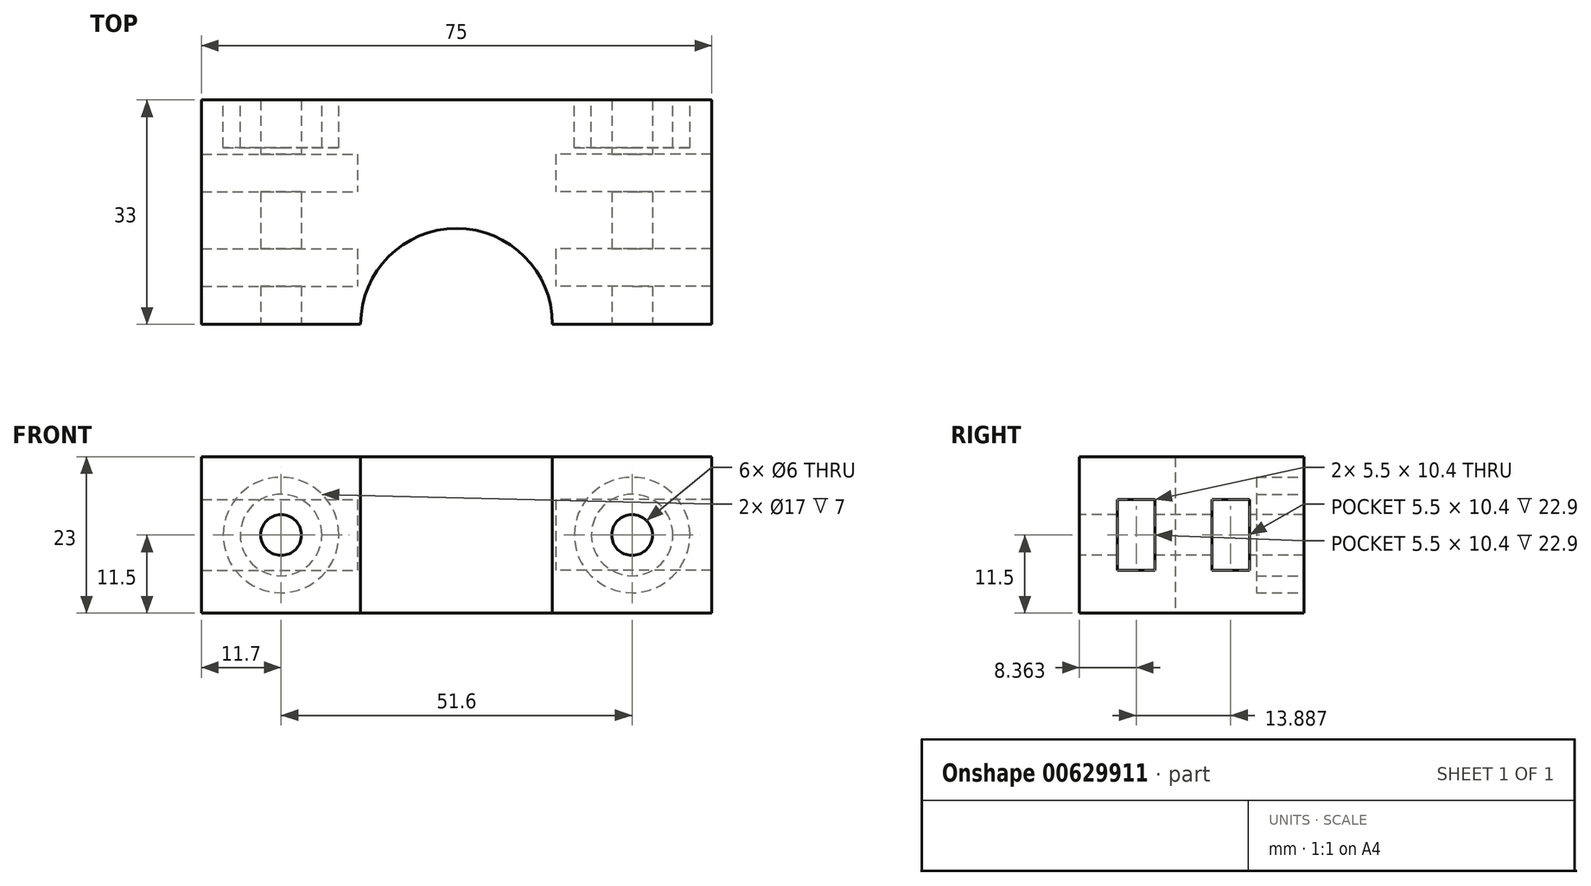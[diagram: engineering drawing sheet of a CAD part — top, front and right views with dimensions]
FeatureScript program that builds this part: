
annotation { "Feature Type Name" : "Feature", "Feature Type Description" : "" }
export const myFeature = defineFeature(function(context is Context, id is Id, definition is map)
    precondition{}
    {
        {
            var Q0;
            Q0=qCreatedBy(makeId("Top.planeOp"),FACE);
            var sketch = newSketch(context, id + "F0", { "sketchPlane" : qUnion([Q0])});
            skLineSegment(sketch, "E0.bottom", {"start": v(-37.5, 33) * mm, "end": v(37.5, 33) * mm});
            skLineSegment(sketch, "E0.top", {"start": v(-37.5, 0) * mm, "end": v(-14.1, 0) * mm});
            skLineSegment(sketch, "E0.left", {"start": v(-37.5, 33) * mm, "end": v(-37.5, 0) * mm});
            skLineSegment(sketch, "E0.right", {"start": v(37.5, 33) * mm, "end": v(37.5, 0) * mm});
            skLineSegment(sketch, "E1", {"start": v(14.1, 0) * mm, "end": v(37.5, 0) * mm});
            skArc(sketch, "E2", {"start": v(14.1, 0) * mm, "mid": v(0, 14.1) * mm, "end": v(-14.1, 0) * mm});
            skSolve(sketch);
        }
        {
            var Q0;
            Q0=makeQuery(id+"F0.imprint","IMPRINT",FACE,{"disambiguationData":[TD([[makeQuery(id+"F0.imprint","IMPRINT",EDGE,{"derivedFrom":sQuery(id+"F0.wireOp",EDGE,"E0.bottom")}),-1.0]])]});
            extrude(context, id + "F1", {"entities" : qUnion([Q0]), "depth" : 23 * mm, "offsetDistance" : 25 * mm});
        }
        {
            var Q0;
            Q0=qCreatedBy(makeId("Right.planeOp"),FACE);
            var sketch = newSketch(context, id + "F2", { "sketchPlane" : qUnion([Q0])});
            skLineSegment(sketch, "E3.bottom", {"start": v(11.11, 16.7) * mm, "end": v(5.61, 16.7) * mm});
            skLineSegment(sketch, "E3.top", {"start": v(11.11, 6.3) * mm, "end": v(5.61, 6.3) * mm});
            skLineSegment(sketch, "E3.left", {"start": v(11.11, 16.7) * mm, "end": v(11.11, 6.3) * mm});
            skLineSegment(sketch, "E3.right", {"start": v(5.61, 16.7) * mm, "end": v(5.61, 6.3) * mm});
            skLineSegment(sketch, "E4.bottom", {"start": v(25, 16.7) * mm, "end": v(19.5, 16.7) * mm});
            skLineSegment(sketch, "E4.top", {"start": v(25, 6.3) * mm, "end": v(19.5, 6.3) * mm});
            skLineSegment(sketch, "E4.left", {"start": v(25, 16.7) * mm, "end": v(25, 6.3) * mm});
            skLineSegment(sketch, "E4.right", {"start": v(19.5, 16.7) * mm, "end": v(19.5, 6.3) * mm});
            skSolve(sketch);
        }
        {
            var Q0;
            Q0=makeQuery(id+"F1.opExtrude","SWEPT_FACE",FACE,{"disambiguationData":[OSD([sQuery(id+"F0.wireOp",EDGE,"E0.top")])]});
            var sketch = newSketch(context, id + "F3", { "sketchPlane" : qUnion([Q0])});
            skLineSegment(sketch, "E5", {"start": v(-14.1, 23) * mm, "end": v(-25.8, 11.5) * mm});
            skLineSegment(sketch, "E6", {"start": v(-37.5, 0) * mm, "end": v(-37.5, 23) * mm});
            skLineSegment(sketch, "E7", {"start": v(-37.5, 23) * mm, "end": v(-14.1, 0) * mm});
            skLineSegment(sketch, "E8", {"start": v(-25.8, 11.5) * mm, "end": v(-37.5, 0) * mm});
            skCircle(sketch, "E9", {"center": v(-25.8, 11.5) * mm, "radius": 3.02 * mm});
            skSolve(sketch);
        }
        {
            var Q0;
            Q0=makeQuery(id+"F1.opExtrude","SWEPT_FACE",FACE,{"disambiguationData":[OSD([sQuery(id+"F0.wireOp",EDGE,"E1")])]});
            var sketch = newSketch(context, id + "F4", { "sketchPlane" : qUnion([Q0])});
            skLineSegment(sketch, "E10", {"start": v(14.1, 23) * mm, "end": v(37.5, 0) * mm});
            skLineSegment(sketch, "E11", {"start": v(37.5, 0) * mm, "end": v(37.5, 23) * mm});
            skLineSegment(sketch, "E12", {"start": v(37.5, 23) * mm, "end": v(14.1, 0) * mm});
            skCircle(sketch, "E13", {"center": v(25.8, 11.5) * mm, "radius": 3 * mm});
            skSolve(sketch);
        }
        {
            var Q0;
            Q0=sQuery(id+"F3.wireOp",VERTEX,"E9.center");
            var Q1;
            Q1=makeQuery(id+"F1.opExtrude","SWEPT_BODY",BODY,{"disambiguationData":[OSD([sQuery(id+"F0.wireOp",EDGE,"E0.bottom"),sQuery(id+"F0.wireOp",EDGE,"E0.top"),sQuery(id+"F0.wireOp",EDGE,"E0.left"),sQuery(id+"F0.wireOp",EDGE,"E0.right"),sQuery(id+"F0.wireOp",EDGE,"E1"),sQuery(id+"F0.wireOp",EDGE,"E2")])]});
            hole(context, id + "F5", {"style" : HoleStyle.SIMPLE, "endStyle" : HoleEndStyle.THROUGH, "holeDiameter" : 6 * mm, "majorDiameter" : 5 * mm, "isTappedThrough" : true, "tappedDepth" : 12 * mm, "tapClearance" : 3, "locations" : qUnion([Q0]), "scope" : qUnion([Q1])});
        }
        {
            var Q0;
            Q0=sQuery(id+"F4.wireOp",VERTEX,"E13.center");
            var Q1;
            Q1=makeQuery(id+"F1.opExtrude","SWEPT_BODY",BODY,{"disambiguationData":[OSD([sQuery(id+"F0.wireOp",EDGE,"E0.bottom"),sQuery(id+"F0.wireOp",EDGE,"E0.top"),sQuery(id+"F0.wireOp",EDGE,"E0.left"),sQuery(id+"F0.wireOp",EDGE,"E0.right"),sQuery(id+"F0.wireOp",EDGE,"E1"),sQuery(id+"F0.wireOp",EDGE,"E2")])]});
            hole(context, id + "F6", {"style" : HoleStyle.SIMPLE, "endStyle" : HoleEndStyle.THROUGH, "holeDiameter" : 6 * mm, "majorDiameter" : 5 * mm, "isTappedThrough" : true, "tappedDepth" : 12 * mm, "tapClearance" : 3, "locations" : qUnion([Q0]), "scope" : qUnion([Q1])});
        }
        {
            var Q0;
            Q0 = qSketchRegion(id + "F2", true);
            extrude(context, id + "F7", {"entities" : qUnion([Q0]), "operationType" : NewBodyOperationType.REMOVE, "depth" : 44.2 * mm, "offsetDistance" : 25 * mm, "hasSecondDirection" : true, "secondDirectionOppositeDirection" : false, "secondDirectionDepth" : 14.6 * mm});
        }
        {
            var Q0;
            Q0=makeQuery(id+"F1.opExtrude","SWEPT_FACE",FACE,{"disambiguationData":[OSD([sQuery(id+"F0.wireOp",EDGE,"E0.bottom")])]});
            var sketch = newSketch(context, id + "F8", { "sketchPlane" : qUnion([Q0])});
            skCircle(sketch, "E14", {"center": v(25.8, 11.5) * mm, "radius": 6 * mm});
            skCircle(sketch, "E15", {"center": v(25.8, 11.5) * mm, "radius": 8.5 * mm});
            skSolve(sketch);
        }
        {
            var Q0;
            Q0=makeQuery(id+"F1.opExtrude","SWEPT_FACE",FACE,{"disambiguationData":[OSD([sQuery(id+"F0.wireOp",EDGE,"E0.bottom")])]});
            var sketch = newSketch(context, id + "F9", { "sketchPlane" : qUnion([Q0])});
            skCircle(sketch, "E16", {"center": v(-25.8, 11.5) * mm, "radius": 6 * mm});
            skCircle(sketch, "E17", {"center": v(-25.8, 11.5) * mm, "radius": 8.5 * mm});
            skSolve(sketch);
        }
        {
            var Q0;
            Q0 = qSketchRegion(id + "F9", true);
            extrude(context, id + "F10", {"entities" : qUnion([Q0]), "operationType" : NewBodyOperationType.REMOVE, "oppositeDirection" : true, "depth" : 7 * mm, "offsetDistance" : 25 * mm});
        }
        {
            var Q0;
            Q0 = qSketchRegion(id + "F8", true);
            extrude(context, id + "F11", {"entities" : qUnion([Q0]), "operationType" : NewBodyOperationType.REMOVE, "oppositeDirection" : true, "depth" : 7 * mm, "offsetDistance" : 25 * mm});
        }
        {
            var Q0;
            Q0 = qSketchRegion(id + "F2", true);
            extrude(context, id + "F12", {"entities" : qUnion([Q0]), "operationType" : NewBodyOperationType.REMOVE, "oppositeDirection" : true, "depth" : 45.4 * mm, "offsetDistance" : 25 * mm, "hasSecondDirection" : true, "secondDirectionOppositeDirection" : true, "secondDirectionDepth" : 14.6 * mm});
        }
    });
